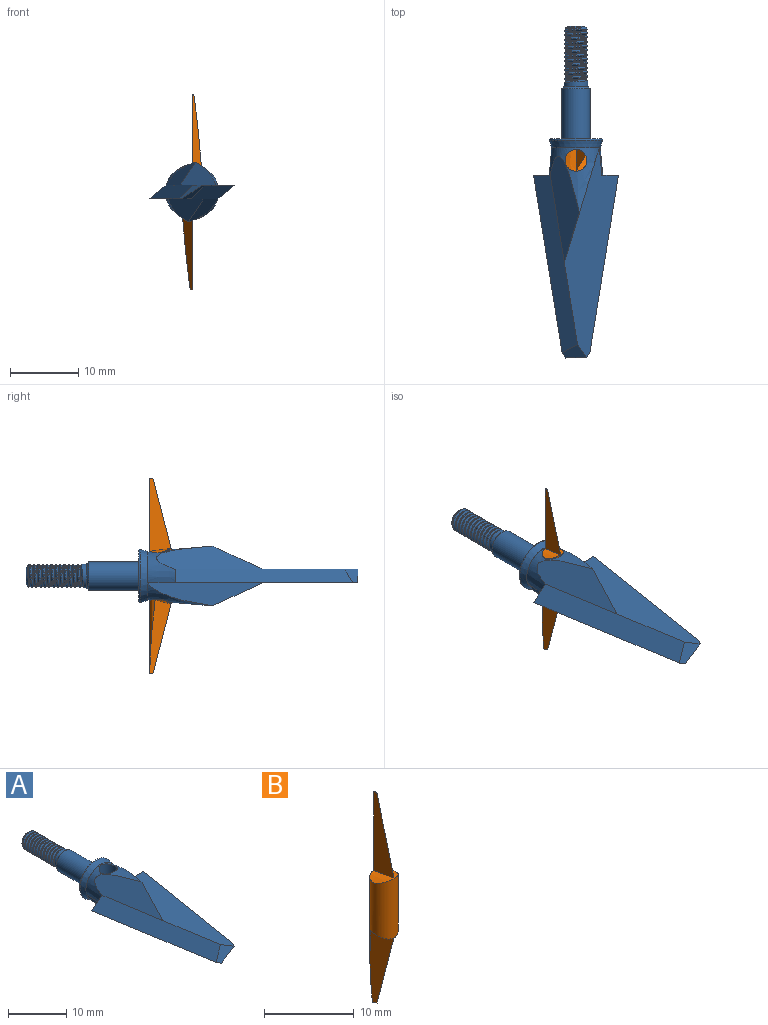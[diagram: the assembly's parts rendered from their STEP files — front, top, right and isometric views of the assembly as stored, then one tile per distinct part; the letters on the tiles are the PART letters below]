
ASSEMBLY  parts=2 mates=1
PART A: 46 faces, bbox 12.4x48.5x8.8 mm
  f0: cylinder r=2.08mm len=7.37mm, axis (0,-1,0), area 96.4mm2, adj f2,f36
  f1: plane 3.66x3.66mm, normal (0,1,0), area 0.9mm2, adj f2,f3
  f2: cone r=1.83mm half-angle=45deg, axis (0,-1,0), area 4.4mm2, adj f0,f1
  f3: cylinder r=1.75mm len=3.51mm, axis (0,-1,0), area 7.4mm2, adj f1,f4,f18,f19,f21
  f4: cylinder r=1.75mm len=3.51mm, axis (0,-1,0), area 1mm2, adj f3,f5,f19,f21
  f5: cylinder r=1.75mm len=3.51mm, axis (0,-1,0), area 1mm2, adj f4,f6,f19,f21
  f6: cylinder r=1.75mm len=3.51mm, axis (0,-1,0), area 1mm2, adj f5,f7,f19,f21
  f7: cylinder r=1.75mm len=3.51mm, axis (0,-1,0), area 1mm2, adj f6,f8,f19,f21
  f8: cylinder r=1.75mm len=3.51mm, axis (0,-1,0), area 1mm2, adj f7,f9,f19,f21
  f9: cylinder r=1.75mm len=3.51mm, axis (0,-1,0), area 1mm2, adj f8,f10,f19,f21
  f10: cylinder r=1.75mm len=3.51mm, axis (0,-1,0), area 1mm2, adj f9,f11,f19,f21
  f11: cylinder r=1.75mm len=3.51mm, axis (0,-1,0), area 1mm2, adj f10,f12,f19,f21
  f12: cylinder r=1.75mm len=3.51mm, axis (0,-1,0), area 1mm2, adj f11,f13,f19,f21
  f13: cylinder r=1.75mm len=3.51mm, axis (0,-1,0), area 1mm2, adj f12,f14,f19,f21
  f14: cylinder r=1.75mm len=3.51mm, axis (0,-1,0), area 1mm2, adj f13,f15,f19,f21
  f15: cylinder r=1.75mm len=1.33mm, axis (0,-1,0), area 0.1mm2, adj f14,f17,f21
  f16: plane 2.49x2.49mm, normal (0,1,0), area 4.9mm2, adj f17
  f17: cone r=1.24mm half-angle=45deg, axis (0,-1,0), area 4.6mm2, adj f15,f16,f19,f20,f21
  f18: plane 0.55x0.27mm, normal (0,0,-1), area 0.1mm2, adj f3,f19,f20,f21
  f19: bspline ~8.47x4.05mm, area 45.1mm2, adj f3,f4,f5,f6,f7,f8,f9,f10
  f20: cylinder r=1.48mm len=8.16mm, axis (0,1,0), area 20.7mm2, adj f17,f18,f19,f21
  f21: bspline ~8.23x4.05mm, area 41.3mm2, adj f3,f4,f5,f6,f7,f8,f9,f10
  f22: cone r=3.56mm half-angle=5deg, axis (0,-1,0), area 33.9mm2, adj f23,f24,f25,f29,f34,f37,f39,f40
  f23: plane 16.75x5.11mm, normal (0.96,-0.29,0), area 34.8mm2, adj f22,f24,f26
  f24: plane 15.44x4.28mm, normal (-0.7,-0.11,0.71), area 49mm2, adj f22,f23,f32,f40
  f25: plane 2.43x2mm, normal (0,1,0), area 2.3mm2, adj f22,f29,f32
  f26: plane 30.74x7.91mm, normal (0,0,1), area 115.5mm2, adj f23,f27,f28,f30,f31,f32,f42
  f27: plane 2.43x2mm, normal (0,1,0), area 2.3mm2, adj f26,f31,f42
  f28: plane 3.55x2.03mm, normal (-0.52,-0.34,0.78), area 5.3mm2, adj f26,f29,f30,f32
  f29: plane 30.74x7.91mm, normal (0,0,-1), area 115.4mm2, adj f22,f25,f28,f30,f31,f32,f43,f44
  f30: plane 3.55x2.03mm, normal (0.52,-0.34,-0.78), area 5.3mm2, adj f26,f28,f29,f31
  f31: plane 25.9x6.43mm, normal (0.63,-0.1,-0.77), area 81mm2, adj f26,f27,f29,f30,f33,f45
  f32: plane 25.9x6.43mm, normal (-0.63,-0.1,0.77), area 81mm2, adj f24,f25,f26,f28,f29,f34
  f33: plane 0.03x0.03mm, normal (0,-1,0), area 0mm2, adj f31,f41,f42
  f34: plane 0.03x0.03mm, normal (0,-1,0), area 0mm2, adj f22,f32,f40
  f35: cone r=3.94mm half-angle=16deg, axis (0,1,0), area 27mm2, adj f37,f38
  f36: plane 7.54x7.54mm, normal (0,1,0), area 31mm2, adj f0,f38
  f37: plane 7.15x7.15mm, normal (0,-1,0), area 0.4mm2, adj f22,f35,f42
  f38: torus R=3.77mm, axis (0,1,0), area 5.7mm2, adj f35,f36
  f39: cylinder r=1.59mm len=7.28mm, axis (0,0,-1), area 72.6mm2, adj f22,f42
  f40: plane 0.1x0.03mm, normal (0,0,1), area 0mm2, adj f22,f24,f34
  f41: plane 0.1x0.03mm, normal (0,0,-1), area 0mm2, adj f33,f42,f45
  f42: cone r=3.56mm half-angle=5deg, axis (0,-1,0), area 33.9mm2, adj f26,f27,f33,f37,f39,f41,f44,f45
  f43: plane 0x0mm, normal (0,-1,0), area 0mm2, adj f29,f44,f45
  f44: plane 16.76x5.11mm, normal (-0.96,-0.29,0), area 34.8mm2, adj f29,f42,f43,f45
  f45: plane 15.46x4.28mm, normal (0.7,-0.11,-0.71), area 49mm2, adj f31,f41,f42,f43,f44
PART B: 11 faces, bbox 3.4x3.2x28.6 mm
  f0: cylinder r=1.59mm len=28.58mm, axis (0,0,-1), area 93.6mm2, adj f1,f2,f3,f4,f5,f6,f7,f8
  f1: plane 0.51x0.27mm, normal (0,0,-1), area 0.1mm2, adj f0,f3,f9
  f2: plane 0.51x0.27mm, normal (0,0,1), area 0.1mm2, adj f0,f4,f7
  f3: plane 10.69x3.18mm, normal (1,0,0), area 19.6mm2, adj f0,f1,f6,f9
  f4: plane 10.69x3.18mm, normal (-1,0,0), area 19.6mm2, adj f0,f2,f5,f7
  f5: cone r=3.56mm half-angle=8deg, axis (0,-1,0), area 4.1mm2, adj f0,f4
  f6: cone r=3.56mm half-angle=8deg, axis (0,-1,0), area 4.1mm2, adj f0,f3
  f7: plane 10.85x3.15mm, normal (0.87,-0.48,0.13), area 18.9mm2, adj f0,f2,f4,f8
  f8: cone r=3.56mm half-angle=8deg, axis (0,-1,0), area 1.6mm2, adj f0,f7
  f9: plane 10.85x3.15mm, normal (-0.87,-0.48,-0.13), area 18.9mm2, adj f0,f1,f3,f10
  f10: cone r=3.56mm half-angle=8deg, axis (0,-1,0), area 1.6mm2, adj f0,f9
PLACE A at identity fixed
PLACE B t=(0,4.06,0)mm
MATE cylindrical A.f39 <-> B.f0  axis (0,0,-1) through (0,2.21,0)mm
